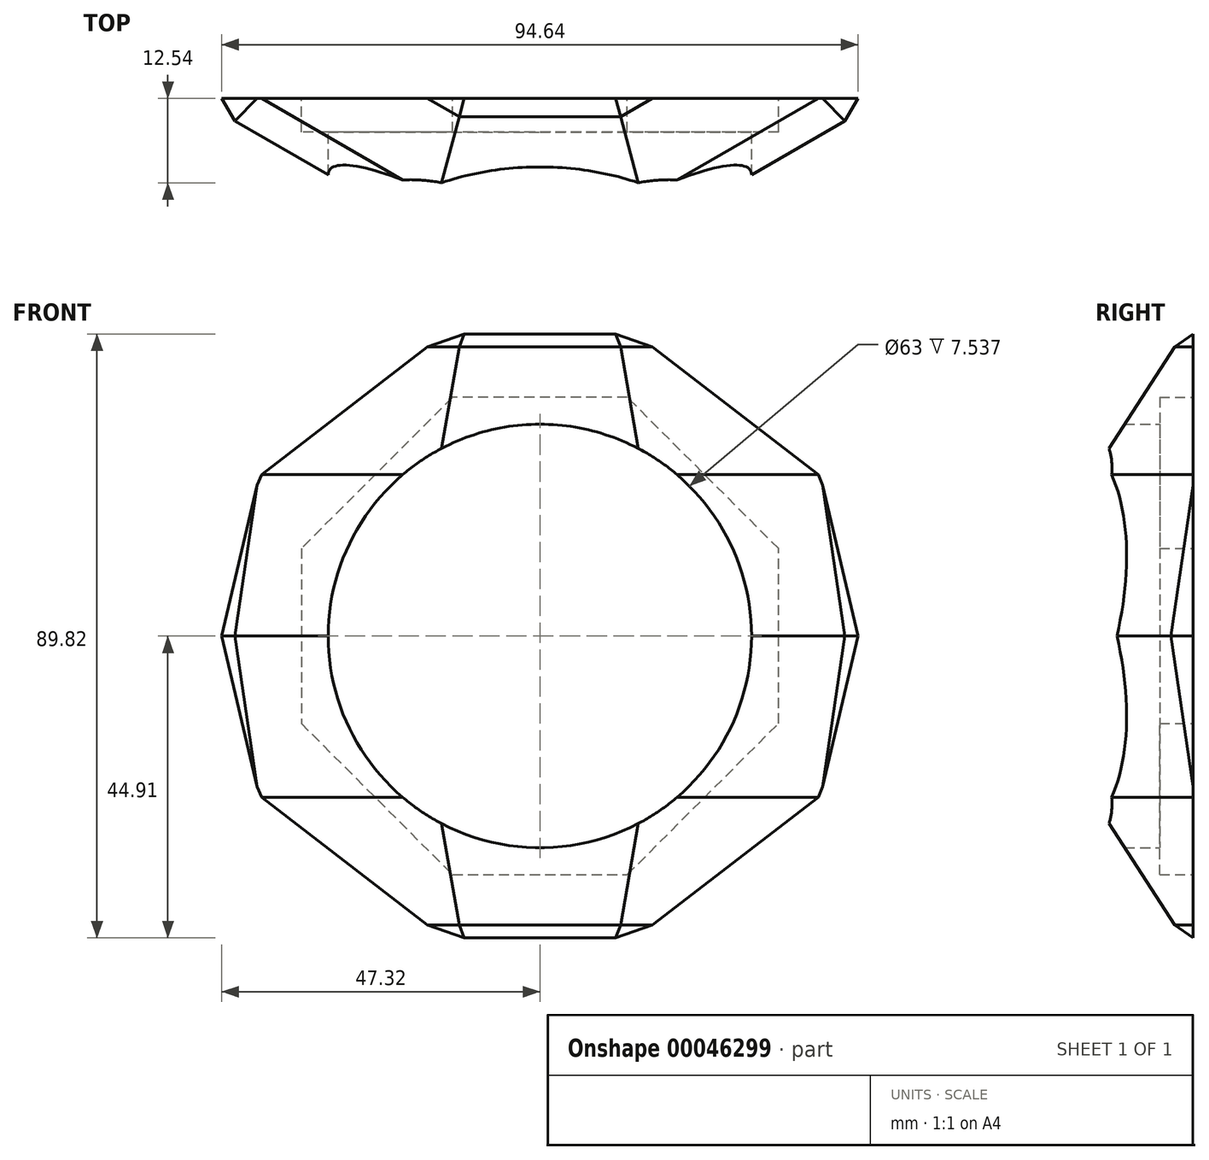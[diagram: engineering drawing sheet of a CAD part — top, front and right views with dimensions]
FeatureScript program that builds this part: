
annotation { "Feature Type Name" : "Feature", "Feature Type Description" : "" }
export const myFeature = defineFeature(function(context is Context, id is Id, definition is map)
    precondition{}
    {
        {
            var Q0;
            Q0=qCreatedBy(makeId("Front.planeOp"),FACE);
            var sketch = newSketch(context, id + "F0", { "sketchPlane" : qUnion([Q0])});
            skLineSegment(sketch, "E0", {"start": v(0, 0) * mm, "end": v(0, 113) * mm});
            skCircle(sketch, "E1", {"center": v(0, 56.5) * mm, "radius": 62.05 * mm});
            skSolve(sketch);
        }
        {
            var Q0;
            Q0=qCreatedBy(makeId("Top.planeOp"),FACE);
            var sketch = newSketch(context, id + "F1", { "sketchPlane" : qUnion([Q0])});
            skCircle(sketch, "E2.cCircle", {"center": v(0, 0) * mm, "radius": 25.5 * mm, "construction": true});
            skLineSegment(sketch, "E2.0", {"start": v(25.5, -6.83) * mm, "end": v(18.67, -18.67) * mm});
            skLineSegment(sketch, "E2.1", {"start": v(18.67, -18.67) * mm, "end": v(6.83, -25.5) * mm});
            skLineSegment(sketch, "E2.2", {"start": v(6.83, -25.5) * mm, "end": v(-6.83, -25.5) * mm});
            skLineSegment(sketch, "E2.3", {"start": v(-6.83, -25.5) * mm, "end": v(-18.67, -18.67) * mm});
            skLineSegment(sketch, "E2.4", {"start": v(-18.67, -18.67) * mm, "end": v(-25.5, -6.83) * mm});
            skLineSegment(sketch, "E2.5", {"start": v(-25.5, -6.83) * mm, "end": v(-25.5, 6.83) * mm});
            skLineSegment(sketch, "E2.6", {"start": v(-25.5, 6.83) * mm, "end": v(-18.67, 18.67) * mm});
            skLineSegment(sketch, "E2.7", {"start": v(-18.67, 18.67) * mm, "end": v(-6.83, 25.5) * mm});
            skLineSegment(sketch, "E2.8", {"start": v(-6.83, 25.5) * mm, "end": v(6.83, 25.5) * mm});
            skLineSegment(sketch, "E2.9", {"start": v(6.83, 25.5) * mm, "end": v(18.67, 18.67) * mm});
            skLineSegment(sketch, "E2.10", {"start": v(18.67, 18.67) * mm, "end": v(25.5, 6.83) * mm});
            skLineSegment(sketch, "E2.11", {"start": v(25.5, 6.83) * mm, "end": v(25.5, -6.83) * mm});
            skPoint(sketch, "E2.0.midPoint", {"position": v(22.08, -12.75) * mm});
            skSolve(sketch);
        }
        {
            var Q0;
            Q0=qSketchRegion(id+"F1",true);
            extrude(context, id + "F2", {"entities" : qUnion([Q0]), "depth" : 13.5 * mm, "hasDraft" : true, "draftAngle" : 55 * degree});
        }
        {
            var Q0;
            Q0=makeQuery(id+"F2.opExtrude","CAP_FACE",FACE,{"disambiguationData":[OSD([sQuery(id+"F1.wireOp",EDGE,"E2.0"),sQuery(id+"F1.wireOp",EDGE,"E2.1"),sQuery(id+"F1.wireOp",EDGE,"E2.2"),sQuery(id+"F1.wireOp",EDGE,"E2.3"),sQuery(id+"F1.wireOp",EDGE,"E2.4"),sQuery(id+"F1.wireOp",EDGE,"E2.5"),sQuery(id+"F1.wireOp",EDGE,"E2.6"),sQuery(id+"F1.wireOp",EDGE,"E2.7"),sQuery(id+"F1.wireOp",EDGE,"E2.8"),sQuery(id+"F1.wireOp",EDGE,"E2.9"),sQuery(id+"F1.wireOp",EDGE,"E2.10"),sQuery(id+"F1.wireOp",EDGE,"E2.11")])],"isStart":false});
            var sketch = newSketch(context, id + "F3", { "sketchPlane" : qUnion([Q0])});
            skLineSegment(sketch, "E3.0", {"start": v(32.78, -32.78) * mm, "end": v(12, -44.78) * mm});
            skLineSegment(sketch, "E4.0", {"start": v(44.78, -12) * mm, "end": v(32.78, -32.78) * mm});
            skLineSegment(sketch, "E5.0", {"start": v(44.78, 12) * mm, "end": v(44.78, -12) * mm});
            skLineSegment(sketch, "E6.0", {"start": v(32.78, 32.78) * mm, "end": v(44.78, 12) * mm});
            skLineSegment(sketch, "E7.0", {"start": v(12, 44.78) * mm, "end": v(32.78, 32.78) * mm});
            skLineSegment(sketch, "E8.0", {"start": v(-12, 44.78) * mm, "end": v(12, 44.78) * mm});
            skLineSegment(sketch, "E9.0", {"start": v(-32.78, 32.78) * mm, "end": v(-12, 44.78) * mm});
            skLineSegment(sketch, "E10.0", {"start": v(-44.78, 12) * mm, "end": v(-32.78, 32.78) * mm});
            skLineSegment(sketch, "E11.0", {"start": v(-44.78, -12) * mm, "end": v(-44.78, 12) * mm});
            skLineSegment(sketch, "E12.0", {"start": v(-32.78, -32.78) * mm, "end": v(-44.78, -12) * mm});
            skLineSegment(sketch, "E13.0", {"start": v(-12, -44.78) * mm, "end": v(-32.78, -32.78) * mm});
            skLineSegment(sketch, "E14.0", {"start": v(12, -44.78) * mm, "end": v(-12, -44.78) * mm});
            skSolve(sketch);
        }
        {
            var Q0;
            Q0=qSketchRegion(id+"F3",true);
            extrude(context, id + "F4", {"entities" : qUnion([Q0]), "operationType" : NewBodyOperationType.ADD, "depth" : 19 * mm, "hasDraft" : true, "draftAngle" : 33 * degree});
        }
        {
            var Q0;
            Q0=makeQuery(id+"F4.opExtrude","CAP_FACE",FACE,{"disambiguationData":[OSD([sQuery(id+"F3.wireOp",EDGE,"E3.0"),sQuery(id+"F3.wireOp",EDGE,"E4.0"),sQuery(id+"F3.wireOp",EDGE,"E5.0"),sQuery(id+"F3.wireOp",EDGE,"E6.0"),sQuery(id+"F3.wireOp",EDGE,"E7.0"),sQuery(id+"F3.wireOp",EDGE,"E8.0"),sQuery(id+"F3.wireOp",EDGE,"E9.0"),sQuery(id+"F3.wireOp",EDGE,"E10.0"),sQuery(id+"F3.wireOp",EDGE,"E11.0"),sQuery(id+"F3.wireOp",EDGE,"E12.0"),sQuery(id+"F3.wireOp",EDGE,"E13.0"),sQuery(id+"F3.wireOp",EDGE,"E14.0")])],"isStart":false});
            var sketch = newSketch(context, id + "F5", { "sketchPlane" : qUnion([Q0])});
            skLineSegment(sketch, "E15.0", {"start": v(41.81, -41.81) * mm, "end": v(15.3, -57.12) * mm});
            skLineSegment(sketch, "E16.0", {"start": v(57.12, -15.3) * mm, "end": v(41.81, -41.81) * mm});
            skLineSegment(sketch, "E17.0", {"start": v(57.12, 15.3) * mm, "end": v(57.12, -15.3) * mm});
            skLineSegment(sketch, "E18.0", {"start": v(41.81, 41.81) * mm, "end": v(57.12, 15.3) * mm});
            skLineSegment(sketch, "E19.0", {"start": v(15.3, 57.12) * mm, "end": v(41.81, 41.81) * mm});
            skLineSegment(sketch, "E20.0", {"start": v(-41.81, 41.81) * mm, "end": v(-15.3, 57.12) * mm});
            skLineSegment(sketch, "E21.0", {"start": v(-57.12, 15.3) * mm, "end": v(-41.81, 41.81) * mm});
            skLineSegment(sketch, "E22.0", {"start": v(-41.81, -41.81) * mm, "end": v(-57.12, -15.3) * mm});
            skLineSegment(sketch, "E23.0", {"start": v(-15.3, -57.12) * mm, "end": v(-41.81, -41.81) * mm});
            skLineSegment(sketch, "E24.0", {"start": v(15.3, -57.12) * mm, "end": v(-15.3, -57.12) * mm});
            skLineSegment(sketch, "E25.0", {"start": v(-57.12, -15.3) * mm, "end": v(-57.12, 15.3) * mm});
            skLineSegment(sketch, "E26.0", {"start": v(-15.3, 57.12) * mm, "end": v(15.3, 57.12) * mm});
            skSolve(sketch);
        }
        {
            var Q0;
            Q0=qSketchRegion(id+"F5",true);
            extrude(context, id + "F6", {"entities" : qUnion([Q0]), "operationType" : NewBodyOperationType.ADD, "depth" : 24 * mm, "hasDraft" : true, "draftAngle" : 11.5 * degree});
        }
        {
            var Q0;
            Q0=makeQuery(id+"F6.opExtrude","CAP_FACE",FACE,{"disambiguationData":[OSD([sQuery(id+"F5.wireOp",EDGE,"E15.0"),sQuery(id+"F5.wireOp",EDGE,"E16.0"),sQuery(id+"F5.wireOp",EDGE,"E17.0"),sQuery(id+"F5.wireOp",EDGE,"E18.0"),sQuery(id+"F5.wireOp",EDGE,"E19.0"),sQuery(id+"F5.wireOp",EDGE,"E20.0"),sQuery(id+"F5.wireOp",EDGE,"E21.0"),sQuery(id+"F5.wireOp",EDGE,"E22.0"),sQuery(id+"F5.wireOp",EDGE,"E23.0"),sQuery(id+"F5.wireOp",EDGE,"E24.0"),sQuery(id+"F5.wireOp",EDGE,"E25.0"),sQuery(id+"F5.wireOp",EDGE,"E26.0")])],"isStart":false});
            var sketch = newSketch(context, id + "F7", { "sketchPlane" : qUnion([Q0])});
            skLineSegment(sketch, "E27.0", {"start": v(16.61, -62) * mm, "end": v(-16.61, -62) * mm});
            skLineSegment(sketch, "E28.0", {"start": v(-16.61, -62) * mm, "end": v(-45.39, -45.39) * mm});
            skLineSegment(sketch, "E29.0", {"start": v(-45.39, -45.39) * mm, "end": v(-62, -16.61) * mm});
            skLineSegment(sketch, "E30.0", {"start": v(45.39, -45.39) * mm, "end": v(16.61, -62) * mm});
            skLineSegment(sketch, "E31.0", {"start": v(62, -16.61) * mm, "end": v(45.39, -45.39) * mm});
            skLineSegment(sketch, "E32.0", {"start": v(62, 16.61) * mm, "end": v(62, -16.61) * mm});
            skLineSegment(sketch, "E33.0", {"start": v(45.39, 45.39) * mm, "end": v(62, 16.61) * mm});
            skLineSegment(sketch, "E34.0", {"start": v(16.61, 62) * mm, "end": v(45.39, 45.39) * mm});
            skLineSegment(sketch, "E35.0", {"start": v(-16.61, 62) * mm, "end": v(16.61, 62) * mm});
            skLineSegment(sketch, "E36.0", {"start": v(-45.39, 45.39) * mm, "end": v(-16.61, 62) * mm});
            skLineSegment(sketch, "E37.0", {"start": v(-62, 16.61) * mm, "end": v(-45.39, 45.39) * mm});
            skLineSegment(sketch, "E38.0", {"start": v(-62, -16.61) * mm, "end": v(-62, 16.61) * mm});
            skSolve(sketch);
        }
        {
            var Q0;
            Q0=qSketchRegion(id+"F7",true);
            extrude(context, id + "F8", {"entities" : qUnion([Q0]), "operationType" : NewBodyOperationType.ADD, "depth" : 24 * mm, "hasDraft" : true, "draftAngle" : 11.5 * degree, "draftPullDirection" : true});
        }
        {
            var Q0;
            Q0=makeQuery(id+"F8.opExtrude","CAP_FACE",FACE,{"disambiguationData":[OSD([sQuery(id+"F7.wireOp",EDGE,"E27.0"),sQuery(id+"F7.wireOp",EDGE,"E28.0"),sQuery(id+"F7.wireOp",EDGE,"E29.0"),sQuery(id+"F7.wireOp",EDGE,"E30.0"),sQuery(id+"F7.wireOp",EDGE,"E31.0"),sQuery(id+"F7.wireOp",EDGE,"E32.0"),sQuery(id+"F7.wireOp",EDGE,"E33.0"),sQuery(id+"F7.wireOp",EDGE,"E34.0"),sQuery(id+"F7.wireOp",EDGE,"E35.0"),sQuery(id+"F7.wireOp",EDGE,"E36.0"),sQuery(id+"F7.wireOp",EDGE,"E37.0"),sQuery(id+"F7.wireOp",EDGE,"E38.0")])],"isStart":false});
            var sketch = newSketch(context, id + "F9", { "sketchPlane" : qUnion([Q0])});
            skLineSegment(sketch, "E39.0", {"start": v(41.81, -41.81) * mm, "end": v(15.3, -57.12) * mm});
            skLineSegment(sketch, "E40.0", {"start": v(57.12, -15.3) * mm, "end": v(41.81, -41.81) * mm});
            skLineSegment(sketch, "E41.0", {"start": v(15.3, -57.12) * mm, "end": v(-15.3, -57.12) * mm});
            skLineSegment(sketch, "E42.0", {"start": v(-15.3, -57.12) * mm, "end": v(-41.81, -41.81) * mm});
            skLineSegment(sketch, "E43.0", {"start": v(-41.81, -41.81) * mm, "end": v(-57.12, -15.3) * mm});
            skLineSegment(sketch, "E44.0", {"start": v(-57.12, -15.3) * mm, "end": v(-57.12, 15.3) * mm});
            skLineSegment(sketch, "E45.0", {"start": v(-57.12, 15.3) * mm, "end": v(-41.81, 41.81) * mm});
            skLineSegment(sketch, "E46.0", {"start": v(-41.81, 41.81) * mm, "end": v(-15.3, 57.12) * mm});
            skLineSegment(sketch, "E47.0", {"start": v(-15.3, 57.12) * mm, "end": v(15.3, 57.12) * mm});
            skLineSegment(sketch, "E48.0", {"start": v(15.3, 57.12) * mm, "end": v(41.81, 41.81) * mm});
            skLineSegment(sketch, "E49.0", {"start": v(41.81, 41.81) * mm, "end": v(57.12, 15.3) * mm});
            skLineSegment(sketch, "E50.0", {"start": v(57.12, 15.3) * mm, "end": v(57.12, -15.3) * mm});
            skSolve(sketch);
        }
        {
            var Q0;
            Q0=qSketchRegion(id+"F9",true);
            extrude(context, id + "F10", {"entities" : qUnion([Q0]), "operationType" : NewBodyOperationType.ADD, "depth" : 19 * mm, "hasDraft" : true, "draftAngle" : 33 * degree, "draftPullDirection" : true});
        }
        {
            var Q0;
            Q0=makeQuery(id+"F10.opExtrude","CAP_FACE",FACE,{"disambiguationData":[OSD([sQuery(id+"F9.wireOp",EDGE,"E39.0"),sQuery(id+"F9.wireOp",EDGE,"E40.0"),sQuery(id+"F9.wireOp",EDGE,"E41.0"),sQuery(id+"F9.wireOp",EDGE,"E42.0"),sQuery(id+"F9.wireOp",EDGE,"E43.0"),sQuery(id+"F9.wireOp",EDGE,"E44.0"),sQuery(id+"F9.wireOp",EDGE,"E45.0"),sQuery(id+"F9.wireOp",EDGE,"E46.0"),sQuery(id+"F9.wireOp",EDGE,"E47.0"),sQuery(id+"F9.wireOp",EDGE,"E48.0"),sQuery(id+"F9.wireOp",EDGE,"E49.0"),sQuery(id+"F9.wireOp",EDGE,"E50.0")])],"isStart":false});
            var sketch = newSketch(context, id + "F11", { "sketchPlane" : qUnion([Q0])});
            skLineSegment(sketch, "E51.0", {"start": v(-12, -44.78) * mm, "end": v(-32.78, -32.78) * mm});
            skLineSegment(sketch, "E52.0", {"start": v(-32.78, -32.78) * mm, "end": v(-44.78, -12) * mm});
            skLineSegment(sketch, "E53.0", {"start": v(-44.78, -12) * mm, "end": v(-44.78, 12) * mm});
            skLineSegment(sketch, "E54.0", {"start": v(-44.78, 12) * mm, "end": v(-32.78, 32.78) * mm});
            skLineSegment(sketch, "E55.0", {"start": v(12, -44.78) * mm, "end": v(-12, -44.78) * mm});
            skLineSegment(sketch, "E56.0", {"start": v(32.78, -32.78) * mm, "end": v(12, -44.78) * mm});
            skLineSegment(sketch, "E57.0", {"start": v(44.78, -12) * mm, "end": v(32.78, -32.78) * mm});
            skLineSegment(sketch, "E58.0", {"start": v(44.78, 12) * mm, "end": v(44.78, -12) * mm});
            skLineSegment(sketch, "E59.0", {"start": v(32.78, 32.78) * mm, "end": v(44.78, 12) * mm});
            skLineSegment(sketch, "E60.0", {"start": v(12, 44.78) * mm, "end": v(32.78, 32.78) * mm});
            skLineSegment(sketch, "E61.0", {"start": v(-12, 44.78) * mm, "end": v(12, 44.78) * mm});
            skLineSegment(sketch, "E62.0", {"start": v(-32.78, 32.78) * mm, "end": v(-12, 44.78) * mm});
            skSolve(sketch);
        }
        {
            var Q0;
            Q0=qSketchRegion(id+"F11",true);
            extrude(context, id + "F12", {"entities" : qUnion([Q0]), "operationType" : NewBodyOperationType.ADD, "depth" : 13.5 * mm, "hasDraft" : true, "draftAngle" : 55 * degree, "draftPullDirection" : true});
        }
        {
            var Q0;
            Q0=qCreatedBy(makeId("Front.planeOp"),FACE);
            var sketch = newSketch(context, id + "F13", { "sketchPlane" : qUnion([Q0])});
            skLineSegment(sketch, "E63", {"start": v(0, 56.62) * mm, "end": v(0, 118.55) * mm, "construction": true});
            skSolve(sketch);
        }
        {
            var Q0;
            Q0=sQuery(id+"F13.wireOp",VERTEX,"E63.end");
            var Q1;
            Q1=makeQuery(id+"F12.opExtrude","CAP_VERTEX",VERTEX,{"disambiguationData":[OSD([sQuery(id+"F11.wireOp",EDGE,"E55.0"),sQuery(id+"F11.wireOp",EDGE,"E56.0")])],"isStart":false});
            var Q2;
            Q2=makeQuery(id+"F12.opExtrude","CAP_VERTEX",VERTEX,{"disambiguationData":[OSD([sQuery(id+"F11.wireOp",EDGE,"E56.0"),sQuery(id+"F11.wireOp",EDGE,"E57.0")])],"isStart":false});
            cPlane(context, id + "F14", {"entities" : qUnion([Q0, Q1, Q2]), "cplaneType" : CPlaneType.THREE_POINT, "offset" : 150 * mm, "width" : 150 * mm, "height" : 150 * mm});
        }
        {
            var Q0;
            Q0=qCreatedBy(id+"F14.planeOp",FACE);
            var sketch = newSketch(context, id + "F15", { "sketchPlane" : qUnion([Q0])});
            skLineSegment(sketch, "E64", {"start": v(-5.52, 4.13) * mm, "end": v(-12.39, -21.96) * mm});
            skLineSegment(sketch, "E65", {"start": v(-12.39, -21.96) * mm, "end": v(6.39, -2.59) * mm});
            skLineSegment(sketch, "E66.0", {"start": v(6.39, -2.59) * mm, "end": v(-5.52, 4.13) * mm});
            skSolve(sketch);
        }
        {
            var Q0;
            Q0=qSketchRegion(id+"F15",true);
            extrude(context, id + "F16", {"entities" : qUnion([Q0]), "endBound" : BoundingType.UP_TO_NEXT, "depth" : 25 * mm});
        }
        {
            var Q0;
            Q0=makeQuery(id+"F16.opExtrude","SWEPT_BODY",BODY,{"disambiguationData":[OSD([sQuery(id+"F15.wireOp",EDGE,"E64"),sQuery(id+"F15.wireOp",EDGE,"E65"),sQuery(id+"F15.wireOp",EDGE,"E66.0")])]});
            var Q1;
            Q1=sQuery(id+"F13.wireOp",EDGE,"E63");
            circularPattern(context, id + "F17", {"entities" : qUnion([Q0]), "axis" : qUnion([Q1]), "angle" : 30 * degree, "instanceCount" : round(12)});
        }
        {
            var Q0;
            Q0=qCreatedBy(makeId("Front.planeOp"),FACE);
            cPlane(context, id + "F18", {"entities" : qUnion([Q0]), "cplaneType" : CPlaneType.OFFSET, "offset" : 42.05 * mm, "width" : 150 * mm, "height" : 150 * mm});
        }
        {
            var Q0;
            Q0=qCreatedBy(id+"F18.planeOp",FACE);
            var sketch = newSketch(context, id + "F19", { "sketchPlane" : qUnion([Q0])});
            skLineSegment(sketch, "E67.bottom", {"start": v(-72.08, 130.04) * mm, "end": v(78.12, 130.04) * mm});
            skLineSegment(sketch, "E67.top", {"start": v(-72.08, -25.73) * mm, "end": v(78.12, -25.73) * mm});
            skLineSegment(sketch, "E67.left", {"start": v(-72.08, 130.04) * mm, "end": v(-72.08, -25.73) * mm});
            skLineSegment(sketch, "E67.right", {"start": v(78.12, 130.04) * mm, "end": v(78.12, -25.73) * mm});
            skSolve(sketch);
        }
        {
            var Q0;
            Q0=makeQuery(id+"F19.imprint","IMPRINT",FACE,{"disambiguationData":[TD([[makeQuery(id+"F19.imprint","IMPRINT",EDGE,{"derivedFrom":sQuery(id+"F19.wireOp",EDGE,"E67.bottom")}),-1.0]])]});
            extrude(context, id + "F20", {"entities" : qUnion([Q0]), "operationType" : NewBodyOperationType.REMOVE, "endBound" : BoundingType.THROUGH_ALL, "oppositeDirection" : true, "depth" : 25 * mm});
        }
        {
            var Q0;
            Q0=makeQuery(id+"F20.boolean.opBoolean","COPY",FACE,{"derivedFrom":makeQuery(id+"F20.opExtrude","CAP_FACE",FACE,{"disambiguationData":[OSD([sQuery(id+"F19.wireOp",EDGE,"E67.bottom"),sQuery(id+"F19.wireOp",EDGE,"E67.top"),sQuery(id+"F19.wireOp",EDGE,"E67.left"),sQuery(id+"F19.wireOp",EDGE,"E67.right")])],"isStart":true})});
            var sketch = newSketch(context, id + "F21", { "sketchPlane" : qUnion([Q0])});
            skCircle(sketch, "E68", {"center": v(0, 56.5) * mm, "radius": 31.5 * mm});
            skLineSegment(sketch, "E69", {"start": v(0, 56.5) * mm, "end": v(0, 101.41) * mm, "construction": true});
            skLineSegment(sketch, "E70", {"start": v(0, 56.5) * mm, "end": v(0, 11.59) * mm, "construction": true});
            skSolve(sketch);
        }
        {
            var Q0;
            Q0 = qSketchRegion(id + "F21", true);
            extrude(context, id + "F22", {"entities" : qUnion([Q0]), "operationType" : NewBodyOperationType.REMOVE, "oppositeDirection" : true, "depth" : 25 * mm});
        }
        {
            var Q0;
            Q0=makeQuery(id+"F20.boolean.opBoolean","COPY",FACE,{"derivedFrom":makeQuery(id+"F20.opExtrude","CAP_FACE",FACE,{"disambiguationData":[OSD([sQuery(id+"F19.wireOp",EDGE,"E67.bottom"),sQuery(id+"F19.wireOp",EDGE,"E67.top"),sQuery(id+"F19.wireOp",EDGE,"E67.left"),sQuery(id+"F19.wireOp",EDGE,"E67.right")])],"isStart":true})});
            var sketch = newSketch(context, id + "F23", { "sketchPlane" : qUnion([Q0])});
            skLineSegment(sketch, "E71", {"start": v(-13, 92) * mm, "end": v(13, 92) * mm});
            skLineSegment(sketch, "E72", {"start": v(13, 92) * mm, "end": v(35.5, 69.5) * mm});
            skLineSegment(sketch, "E73", {"start": v(35.5, 69.5) * mm, "end": v(35.5, 43.5) * mm});
            skLineSegment(sketch, "E74", {"start": v(35.5, 43.5) * mm, "end": v(13, 21) * mm});
            skLineSegment(sketch, "E75", {"start": v(13, 21) * mm, "end": v(-13, 21) * mm});
            skLineSegment(sketch, "E76", {"start": v(-13, 21) * mm, "end": v(-35.5, 43.5) * mm});
            skLineSegment(sketch, "E77", {"start": v(-35.5, 43.5) * mm, "end": v(-35.5, 69.5) * mm});
            skLineSegment(sketch, "E78", {"start": v(-35.5, 69.5) * mm, "end": v(-13, 92) * mm});
            skLineSegment(sketch, "E79", {"start": v(0, 0) * mm, "end": v(0, 113) * mm, "construction": true});
            skLineSegment(sketch, "E80", {"start": v(0, 56.5) * mm, "end": v(35.5, 56.5) * mm});
            skSolve(sketch);
        }
        {
            var Q0;
            Q0=makeQuery(id+"F23.imprint","IMPRINT",FACE,{"disambiguationData":[TD([[makeQuery(id+"F23.imprint","IMPRINT",EDGE,{"derivedFrom":sQuery(id+"F23.wireOp",EDGE,"E71")}),-1.0]])]});
            extrude(context, id + "F24", {"entities" : qUnion([Q0]), "operationType" : NewBodyOperationType.REMOVE, "oppositeDirection" : true, "depth" : 5 * mm});
        }
    });
